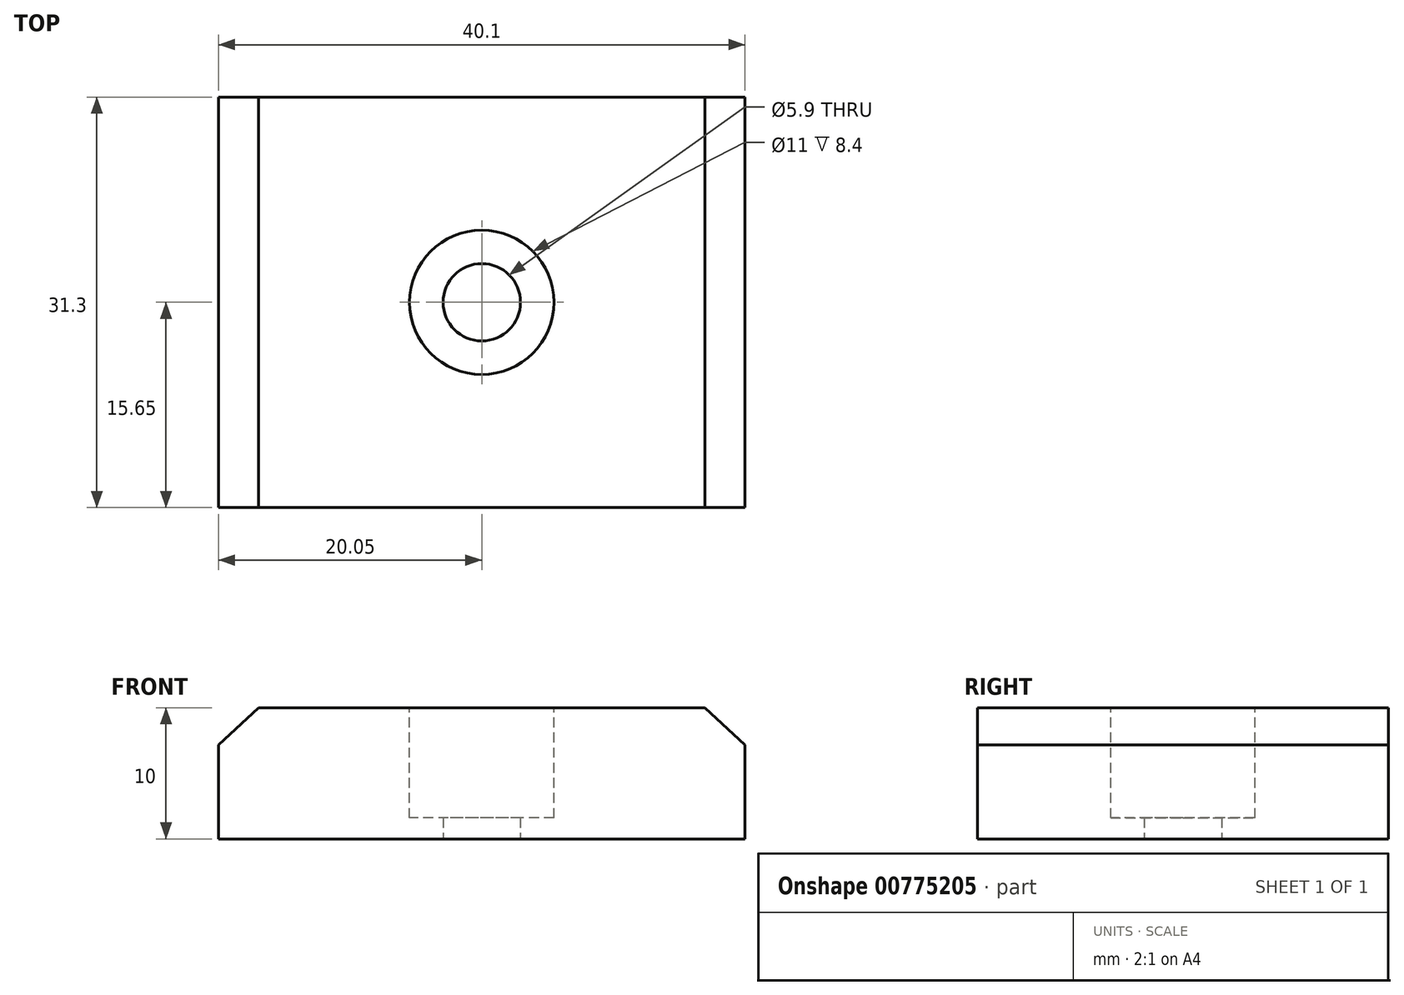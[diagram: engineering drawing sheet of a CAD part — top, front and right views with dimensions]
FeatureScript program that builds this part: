
annotation { "Feature Type Name" : "Feature", "Feature Type Description" : "" }
export const myFeature = defineFeature(function(context is Context, id is Id, definition is map)
    precondition{}
    {
        {
            var Q0;
            Q0=qCreatedBy(makeId("Top.planeOp"),FACE);
            var sketch = newSketch(context, id + "F0", { "sketchPlane" : qUnion([Q0])});
            skLineSegment(sketch, "E0.bottom", {"start": v(20.05, -15.65) * mm, "end": v(-20.05, -15.65) * mm});
            skLineSegment(sketch, "E0.top", {"start": v(20.05, 15.65) * mm, "end": v(-20.05, 15.65) * mm});
            skLineSegment(sketch, "E0.left", {"start": v(20.05, -15.65) * mm, "end": v(20.05, 15.65) * mm});
            skLineSegment(sketch, "E0.right", {"start": v(-20.05, -15.65) * mm, "end": v(-20.05, 15.65) * mm});
            skPoint(sketch, "E0.middle", {"position": v(0, 0) * mm});
            skSolve(sketch);
        }
        {
            var Q0;
            Q0=makeQuery(id+"F0.imprint","IMPRINT",FACE,{"disambiguationData":[TD([[makeQuery(id+"F0.imprint","IMPRINT",EDGE,{"derivedFrom":sQuery(id+"F0.wireOp",EDGE,"E0.bottom")}),-1.0]])]});
            extrude(context, id + "F1", {"entities" : qUnion([Q0]), "depth" : 2.65 * mm, "offsetDistance" : 25 * mm});
        }
        {
            var Q0;
            Q0=makeQuery(id+"F1.opExtrude","CAP_FACE",FACE,{"disambiguationData":[OSD([sQuery(id+"F0.wireOp",EDGE,"E0.bottom"),sQuery(id+"F0.wireOp",EDGE,"E0.top"),sQuery(id+"F0.wireOp",EDGE,"E0.left"),sQuery(id+"F0.wireOp",EDGE,"E0.right")])],"isStart":false});
            var sketch = newSketch(context, id + "F2", { "sketchPlane" : qUnion([Q0])});
            skLineSegment(sketch, "E1.bottom", {"start": v(-17, 15.65) * mm, "end": v(17, 15.65) * mm});
            skLineSegment(sketch, "E1.top", {"start": v(-17, -15.65) * mm, "end": v(17, -15.65) * mm});
            skLineSegment(sketch, "E1.left", {"start": v(-17, 15.65) * mm, "end": v(-17, -15.65) * mm});
            skLineSegment(sketch, "E1.right", {"start": v(17, 15.65) * mm, "end": v(17, -15.65) * mm});
            skPoint(sketch, "E1.middle", {"position": v(0, 0) * mm});
            skSolve(sketch);
        }
        {
            var Q0;
            Q0=makeQuery(id+"F2.imprint","IMPRINT",FACE,{"disambiguationData":[TD([[makeQuery(id+"F2.imprint","IMPRINT",EDGE,{"derivedFrom":sQuery(id+"F2.wireOp",EDGE,"E1.bottom")}),1.0]])]});
            extrude(context, id + "F3", {"entities" : qUnion([Q0]), "operationType" : NewBodyOperationType.ADD, "depth" : 2.85 * mm, "offsetDistance" : 25 * mm});
        }
        {
            var Q0;
            Q0=makeQuery(id+"F3.boolean.opBoolean","MERGE",FACE,{"derivedFrom":[makeQuery(id+"F1.opExtrude","SWEPT_FACE",FACE,{"disambiguationData":[OSD([sQuery(id+"F0.wireOp",EDGE,"E0.bottom")])]}),makeQuery(id+"F3.opExtrude","SWEPT_FACE",FACE,{"disambiguationData":[OSD([sQuery(id+"F2.wireOp",EDGE,"E1.top")])]})]});
            var sketch = newSketch(context, id + "F4", { "sketchPlane" : qUnion([Q0])});
            skLineSegment(sketch, "E2", {"start": v(-20.05, 2.65) * mm, "end": v(-17, 5.5) * mm});
            skLineSegment(sketch, "E3", {"start": v(17, 5.5) * mm, "end": v(20.05, 2.65) * mm});
            skSolve(sketch);
        }
        {
            var Q0;
            Q0=makeQuery(id+"F4.imprint","IMPRINT",FACE,{"disambiguationData":[TD([[makeQuery(id+"F4.imprint","IMPRINT",EDGE,{"derivedFrom":sQuery(id+"F4.wireOp",EDGE,"E3")}),-1.0]])]});
            var Q1;
            Q1=makeQuery(id+"F4.imprint","IMPRINT",FACE,{"disambiguationData":[TD([[makeQuery(id+"F4.imprint","IMPRINT",EDGE,{"derivedFrom":sQuery(id+"F4.wireOp",EDGE,"E2")}),-1.0]])]});
            extrude(context, id + "F5", {"entities" : qUnion([Q0, Q1]), "operationType" : NewBodyOperationType.ADD, "oppositeDirection" : true, "depth" : 31.3 * mm, "offsetDistance" : 25 * mm});
        }
        {
            var Q0;
            Q0=makeQuery(id+"F1.opExtrude","CAP_FACE",FACE,{"disambiguationData":[OSD([sQuery(id+"F0.wireOp",EDGE,"E0.bottom"),sQuery(id+"F0.wireOp",EDGE,"E0.top"),sQuery(id+"F0.wireOp",EDGE,"E0.left"),sQuery(id+"F0.wireOp",EDGE,"E0.right")])],"isStart":true});
            extrude(context, id + "F6", {"entities" : qUnion([Q0]), "operationType" : NewBodyOperationType.ADD, "depth" : 4.5 * mm, "offsetDistance" : 25 * mm});
        }
        {
            var Q0;
            Q0=makeQuery(id+"F6.opExtrude","CAP_FACE",FACE,{"disambiguationData":[OSD([sQuery(id+"F0.wireOp",EDGE,"E0.bottom"),sQuery(id+"F0.wireOp",EDGE,"E0.top"),sQuery(id+"F0.wireOp",EDGE,"E0.left"),sQuery(id+"F0.wireOp",EDGE,"E0.right")])],"isStart":false});
            var sketch = newSketch(context, id + "F7", { "sketchPlane" : qUnion([Q0])});
            skCircle(sketch, "E4", {"center": v(0, 0) * mm, "radius": 2.95 * mm});
            skSolve(sketch);
        }
        {
            var Q0;
            Q0=makeQuery(id+"F7.imprint","IMPRINT",FACE,{"disambiguationData":[TD([[makeQuery(id+"F7.imprint","IMPRINT",EDGE,{"derivedFrom":sQuery(id+"F7.wireOp",EDGE,"E4")}),1.0]])]});
            extrude(context, id + "F8", {"entities" : qUnion([Q0]), "operationType" : NewBodyOperationType.REMOVE, "oppositeDirection" : true, "depth" : 25 * mm, "offsetDistance" : 25 * mm});
        }
        {
            var Q0;
            Q0=makeQuery(id+"F3.opExtrude","CAP_FACE",FACE,{"disambiguationData":[OSD([sQuery(id+"F2.wireOp",EDGE,"E1.bottom"),sQuery(id+"F2.wireOp",EDGE,"E1.top"),sQuery(id+"F2.wireOp",EDGE,"E1.left"),sQuery(id+"F2.wireOp",EDGE,"E1.right")])],"isStart":false});
            var sketch = newSketch(context, id + "F9", { "sketchPlane" : qUnion([Q0])});
            skCircle(sketch, "E5", {"center": v(0, 0) * mm, "radius": 5.5 * mm});
            skSolve(sketch);
        }
        {
            var Q0;
            Q0=makeQuery(id+"F9.imprint","IMPRINT",FACE,{"disambiguationData":[TD([[makeQuery(id+"F9.imprint","IMPRINT",EDGE,{"derivedFrom":sQuery(id+"F9.wireOp",EDGE,"E5")}),1.0]])]});
            extrude(context, id + "F10", {"entities" : qUnion([Q0]), "operationType" : NewBodyOperationType.REMOVE, "oppositeDirection" : true, "depth" : 8.4 * mm, "offsetDistance" : 25 * mm});
        }
    });
